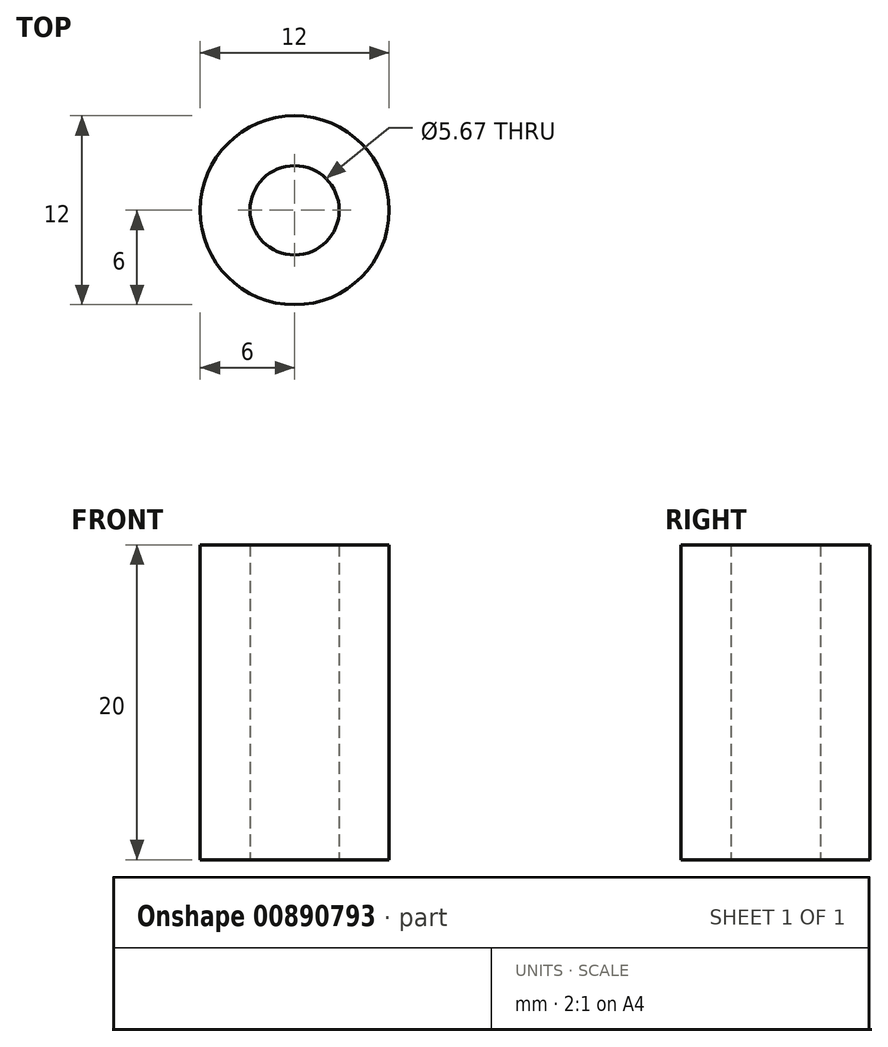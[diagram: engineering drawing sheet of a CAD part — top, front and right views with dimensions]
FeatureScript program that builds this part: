
annotation { "Feature Type Name" : "Feature", "Feature Type Description" : "" }
export const myFeature = defineFeature(function(context is Context, id is Id, definition is map)
    precondition{}
    {
        {
            var Q0;
            Q0=qCreatedBy(makeId("Top.planeOp"),FACE);
            var sketch = newSketch(context, id + "F0", { "sketchPlane" : qUnion([Q0])});
            skCircle(sketch, "E0", {"center": v(0, 0) * mm, "radius": 6 * mm});
            skCircle(sketch, "E1", {"center": v(0, 0) * mm, "radius": 2.83 * mm});
            skSolve(sketch);
        }
        {
            var Q0;
            Q0=makeQuery(id+"F0.imprint","IMPRINT",FACE,{"disambiguationData":[TD([[makeQuery(id+"F0.imprint","IMPRINT",EDGE,{"derivedFrom":sQuery(id+"F0.wireOp",EDGE,"E0")}),1.0]])]});
            extrude(context, id + "F1", {"entities" : qUnion([Q0]), "depth" : 20 * mm, "offsetDistance" : 25 * mm});
        }
    });
